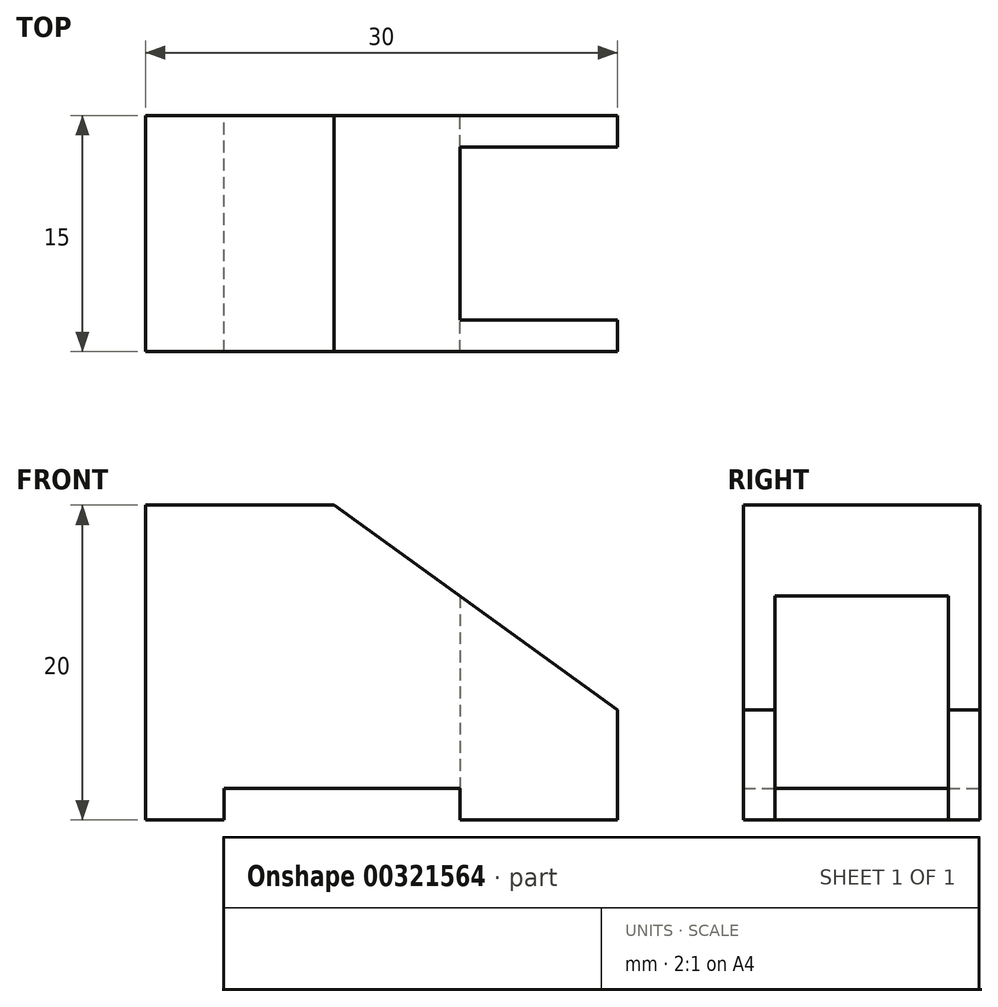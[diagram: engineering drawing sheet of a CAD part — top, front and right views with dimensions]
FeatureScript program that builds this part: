
annotation { "Feature Type Name" : "Feature", "Feature Type Description" : "" }
export const myFeature = defineFeature(function(context is Context, id is Id, definition is map)
    precondition{}
    {
        {
            var Q0;
            Q0=qCreatedBy(makeId("Front.planeOp"),FACE);
            var sketch = newSketch(context, id + "F0", { "sketchPlane" : qUnion([Q0])});
            skLineSegment(sketch, "E0", {"start": v(0, 0) * mm, "end": v(0, 20) * mm});
            skLineSegment(sketch, "E1", {"start": v(0, 20) * mm, "end": v(12, 20) * mm});
            skLineSegment(sketch, "E2", {"start": v(12, 20) * mm, "end": v(30, 7) * mm});
            skLineSegment(sketch, "E3", {"start": v(30, 7) * mm, "end": v(30, 0) * mm});
            skLineSegment(sketch, "E4", {"start": v(30, 0) * mm, "end": v(20, 0) * mm});
            skLineSegment(sketch, "E5", {"start": v(20, 0) * mm, "end": v(20, 2) * mm});
            skLineSegment(sketch, "E6", {"start": v(20, 2) * mm, "end": v(5, 2) * mm});
            skLineSegment(sketch, "E7", {"start": v(5, 2) * mm, "end": v(5, 0) * mm});
            skLineSegment(sketch, "E8", {"start": v(5, 0) * mm, "end": v(0, 0) * mm});
            skSolve(sketch);
        }
        {
            var Q0;
            Q0 = qSketchRegion(id + "F0", true);
            extrude(context, id + "F1", {"entities" : qUnion([Q0]), "depth" : 15 * mm});
        }
        {
            var Q0;
            Q0=qCreatedBy(makeId("Top.planeOp"),FACE);
            var sketch = newSketch(context, id + "F2", { "sketchPlane" : qUnion([Q0])});
            skLineSegment(sketch, "E9.0", {"start": v(30, -13) * mm, "end": v(30, -2) * mm});
            skLineSegment(sketch, "E10", {"start": v(30, -2) * mm, "end": v(20, -2) * mm});
            skLineSegment(sketch, "E11", {"start": v(20, -2) * mm, "end": v(20, -13) * mm});
            skLineSegment(sketch, "E12", {"start": v(20, -13) * mm, "end": v(30, -13) * mm});
            skPoint(sketch, "E13.orphan", {"position": v(30, 0) * mm});
            skPoint(sketch, "E14.orphan", {"position": v(30, -15) * mm});
            skSolve(sketch);
        }
        {
            var Q0;
            Q0 = qSketchRegion(id + "F2", true);
            extrude(context, id + "F3", {"entities" : qUnion([Q0]), "operationType" : NewBodyOperationType.REMOVE, "endBound" : BoundingType.THROUGH_ALL, "depth" : 25 * mm});
        }
    });
